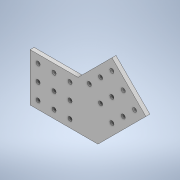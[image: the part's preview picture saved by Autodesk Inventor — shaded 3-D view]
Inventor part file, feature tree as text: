
AUTODESK INVENTOR PART (.ipt)
format: ipt  version: 2020 (Build 240168000, 168)  size: 143,872 bytes
history: native  units: in
note: dims shown in document units (in); Inventor stores cm internally (conversion verified against a paired STEP export)
features: extrude x1, sketch x1
ambient origin geometry x8: Origin, YZ Plane, XZ Plane, XY Plane, X Axis, Y Axis, Z Axis, Center Point
bodies: Solid1 (feature_tree)
feature tree (2):
  extrude  "Extrusion1"  Depth=3.0in
  sketch  "Sketch1"  dims[d5=3.0in d7=3.0in d8=135.0deg d11=3.0in d12=3.0in d13=3.0in d14=0.256in d15=0.5in d16=0.5in d17=1.1811in d19=1.0in d20=1.1811in d22=1.0in d25=0.256in d26=0.5in d27=0.5in d28=1.1811in d30=1.0in d31=1.1811in d33=1.0in d36=0.25in d37=0.0in]
